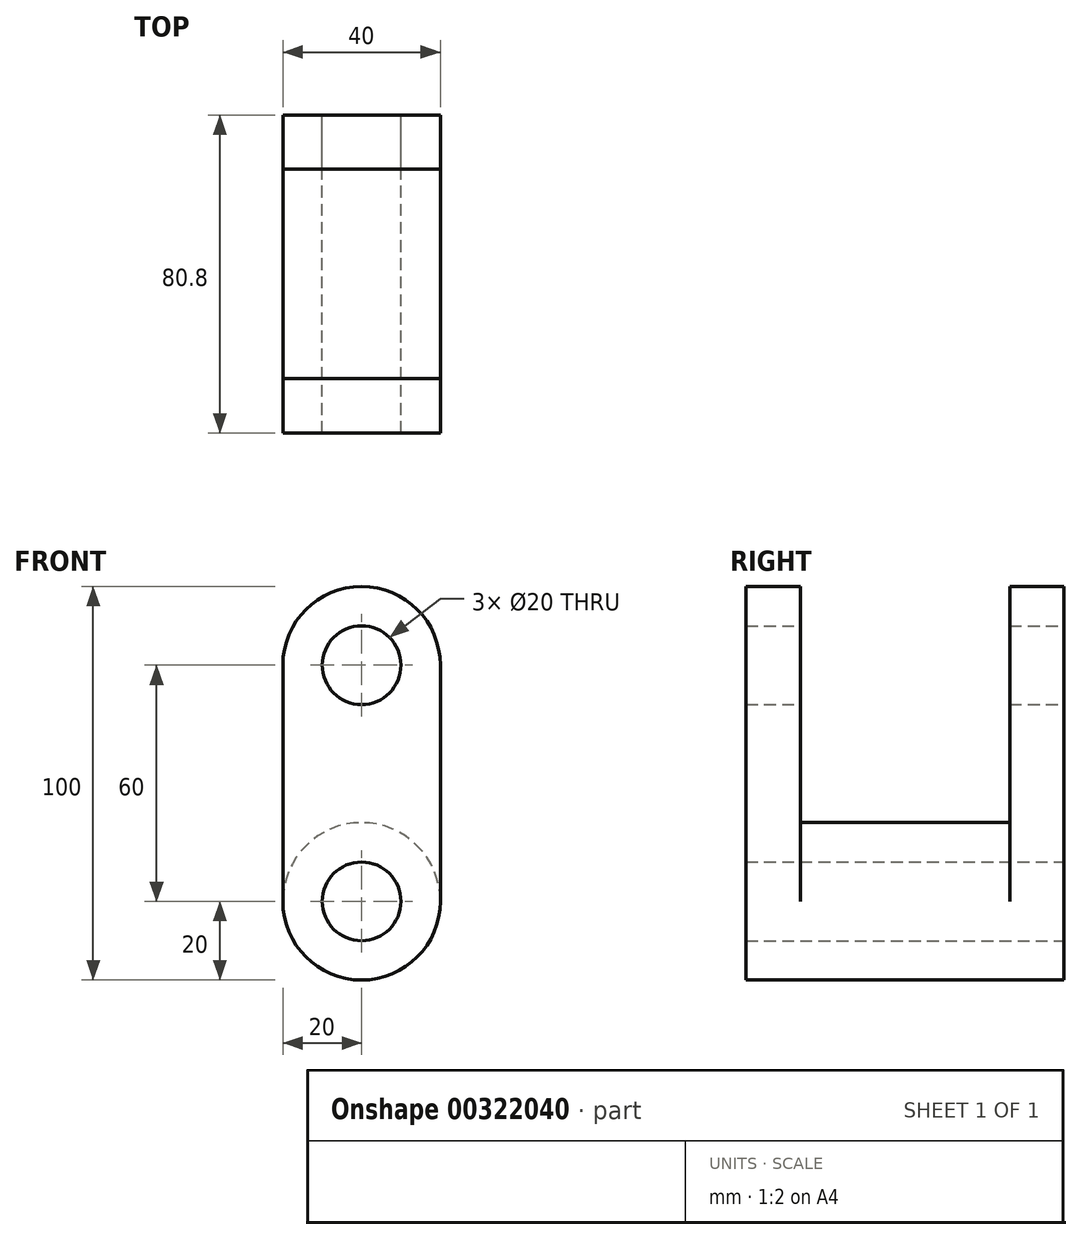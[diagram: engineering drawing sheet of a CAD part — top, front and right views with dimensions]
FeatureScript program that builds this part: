
annotation { "Feature Type Name" : "Feature", "Feature Type Description" : "" }
export const myFeature = defineFeature(function(context is Context, id is Id, definition is map)
    precondition{}
    {
        {
            var Q0;
            Q0=qCreatedBy(makeId("Front.planeOp"),FACE);
            var sketch = newSketch(context, id + "F0", { "sketchPlane" : qUnion([Q0])});
            skLineSegment(sketch, "E0", {"start": v(20, 0) * mm, "end": v(20, 60) * mm});
            skLineSegment(sketch, "E1", {"start": v(-20, 60) * mm, "end": v(-20, 0) * mm});
            skCircle(sketch, "E2", {"center": v(0, 0) * mm, "radius": 20 * mm});
            skArc(sketch, "E3", {"start": v(20, 60) * mm, "mid": v(0, 80) * mm, "end": v(-20, 60) * mm});
            skCircle(sketch, "E4", {"center": v(0, 60) * mm, "radius": 10 * mm});
            skCircle(sketch, "E5", {"center": v(0, 0) * mm, "radius": 10 * mm});
            skSolve(sketch);
        }
        {
            var Q0;
            {var subQ1=sQuery(id+"F0.wireOp",EDGE,"E0");Q0=makeQuery(id+"F0.imprint","IMPRINT",FACE,{"disambiguationData":[TD([[makeQuery(id+"F0.imprint","IMPRINT",EDGE,{"derivedFrom":subQ1}),1.0]])]});}
            var Q1;
            Q1=makeQuery(id+"F0.imprint","IMPRINT",FACE,{"disambiguationData":[TD([[makeQuery(id+"F0.imprint","IMPRINT",EDGE,{"derivedFrom":sQuery(id+"F0.wireOp",EDGE,"E5")}),-1.0]])]});
            extrude(context, id + "F1", {"entities" : qUnion([Q0, Q1]), "endBound" : BoundingType.SYMMETRIC, "depth" : 80.8 * mm});
        }
        {
            var Q0;
            {var subQ1=sQuery(id+"F0.wireOp",EDGE,"E0");Q0=makeQuery(id+"F0.imprint","IMPRINT",FACE,{"disambiguationData":[TD([[makeQuery(id+"F0.imprint","IMPRINT",EDGE,{"derivedFrom":subQ1}),1.0]])]});}
            extrude(context, id + "F2", {"entities" : qUnion([Q0]), "operationType" : NewBodyOperationType.REMOVE, "endBound" : BoundingType.SYMMETRIC, "oppositeDirection" : true, "depth" : 53.2 * mm});
        }
    });
